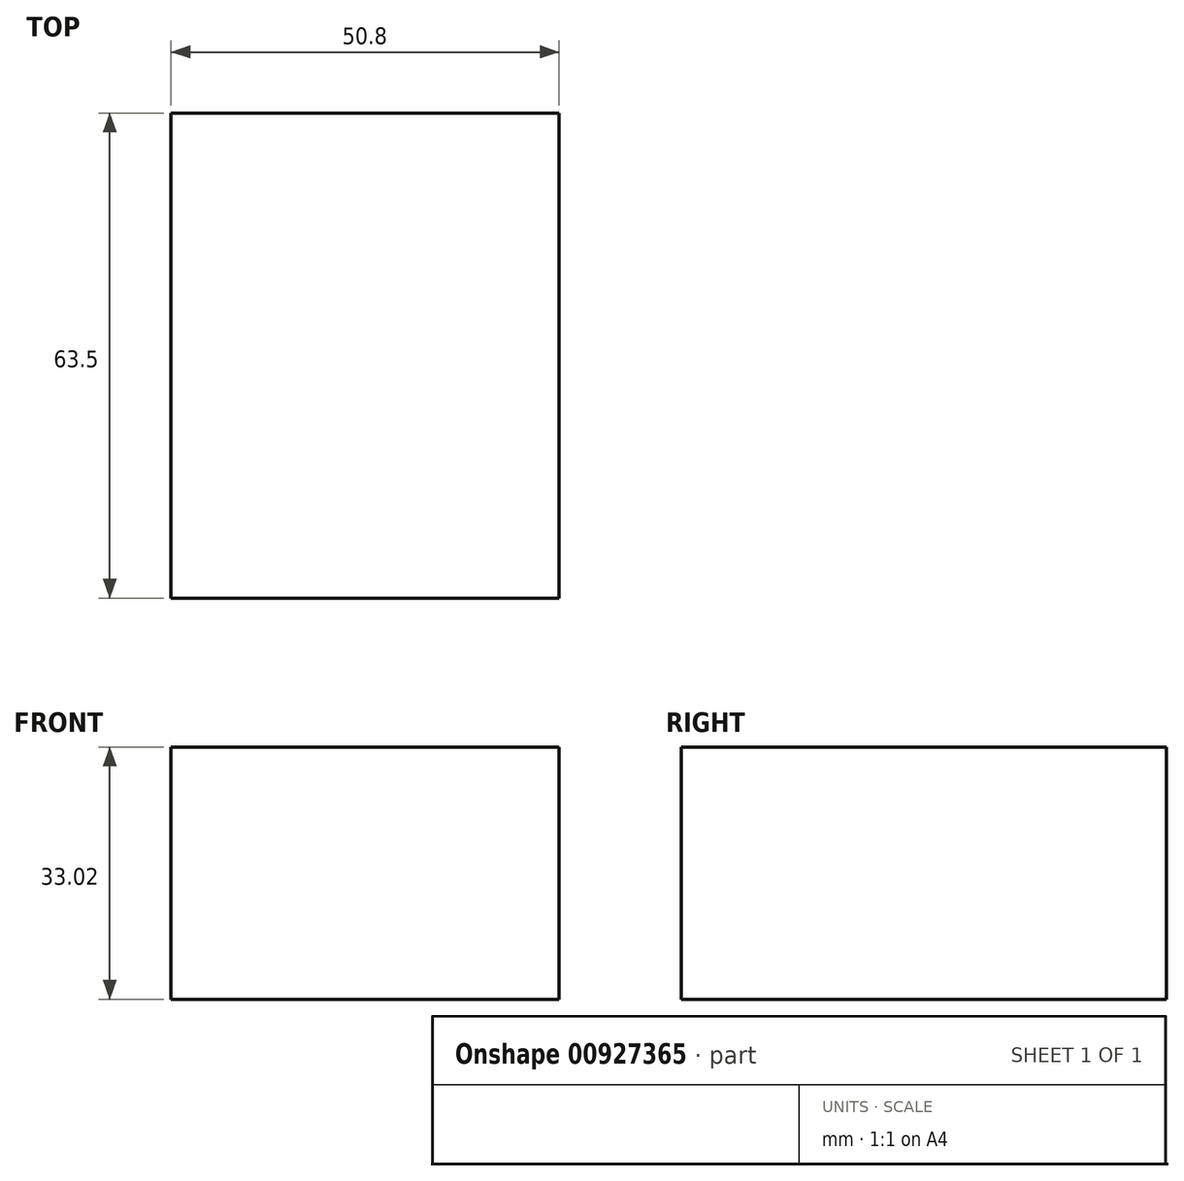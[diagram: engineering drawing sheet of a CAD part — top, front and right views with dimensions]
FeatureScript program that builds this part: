
annotation { "Feature Type Name" : "Feature", "Feature Type Description" : "" }
export const myFeature = defineFeature(function(context is Context, id is Id, definition is map)
    precondition{}
    {
        {
            var Q0;
            Q0=qCreatedBy(makeId("Top.planeOp"),FACE);
            var sketch = newSketch(context, id + "F0", { "sketchPlane" : qUnion([Q0])});
            skLineSegment(sketch, "E0.bottom", {"start": v(5.77, 0) * mm, "end": v(56.57, 0) * mm});
            skLineSegment(sketch, "E0.top", {"start": v(5.77, 63.5) * mm, "end": v(56.57, 63.5) * mm});
            skLineSegment(sketch, "E0.left", {"start": v(5.77, 0) * mm, "end": v(5.77, 63.5) * mm});
            skLineSegment(sketch, "E0.right", {"start": v(56.57, 0) * mm, "end": v(56.57, 63.5) * mm});
            skSolve(sketch);
        }
        {
            var Q0;
            Q0 = qSketchRegion(id + "F0", true);
            extrude(context, id + "F1", {"entities" : qUnion([Q0]), "depth" : 7.62 * mm, "offsetDistance" : 25.4 * mm});
        }
        {
            var Q0;
            Q0=makeQuery(id+"F1.opExtrude","CAP_FACE",FACE,{"disambiguationData":[OSD([sQuery(id+"F0.wireOp",EDGE,"E0.bottom"),sQuery(id+"F0.wireOp",EDGE,"E0.top"),sQuery(id+"F0.wireOp",EDGE,"E0.left"),sQuery(id+"F0.wireOp",EDGE,"E0.right")])],"isStart":false});
            var sketch = newSketch(context, id + "F2", { "sketchPlane" : qUnion([Q0])});
            skSolve(sketch);
        }
        {
            var Q0;
            Q0=makeQuery(id+"F2.imprint","IMPRINT",FACE,{"disambiguationData":[TD([[makeQuery(id+"F2.imprint","IMPRINT",EDGE,{"derivedFrom":makeQuery(id+"F1.opExtrude","CAP_EDGE",EDGE,{"disambiguationData":[OSD([sQuery(id+"F0.wireOp",EDGE,"E0.bottom")])],"isStart":false})}),1.0]])]});
            var sketch = newSketch(context, id + "F3", { "sketchPlane" : qUnion([Q0])});
            skText(sketch, "E1", { "text": "A", "fontName": "OpenSans-Italic.ttf"});
            skText(sketch, "E2", { "text": "M", "fontName": "OpenSans-Regular.ttf"});
            skText(sketch, "E3", { "text": "P", "fontName": "OpenSans-Regular.ttf"});
            const initialGuessF3  = {"E1": [0.01656, 0.0039, 1, 0, 0.01285], "E2": [0.0278, 0.00447, 1, 0, 0.01227], "E3": [0.04263, 0.00447, 1, 0, 0.01227]};
            skSetInitialGuess(sketch, initialGuessF3);
            skSolve(sketch);
        }
        {
            var Q0;
            Q0=makeQuery(id+"F2.imprint","IMPRINT",FACE,{"disambiguationData":[TD([[makeQuery(id+"F2.imprint","IMPRINT",EDGE,{"derivedFrom":makeQuery(id+"F1.opExtrude","CAP_EDGE",EDGE,{"disambiguationData":[OSD([sQuery(id+"F0.wireOp",EDGE,"E0.bottom")])],"isStart":false})}),1.0]])]});
            var Q1;
            Q1 = qSketchRegion(id + "F3", true);
            var Q2;
            Q2=makeQuery(id+"F3.imprint","IMPRINT",FACE,{"disambiguationData":[TD([[makeQuery(id+"F3.imprint","IMPRINT",EDGE,{"derivedFrom":sQuery(id+"F3.wireOp",EDGE,"E1.sketch_text.stroke-0")}),-1.0]])]});
            var Q3;
            Q3=makeQuery(id+"F3.imprint","IMPRINT",FACE,{"disambiguationData":[TD([[makeQuery(id+"F3.imprint","IMPRINT",EDGE,{"derivedFrom":sQuery(id+"F3.wireOp",EDGE,"E1.sketch_text.stroke-8")}),1.0]])]});
            var Q4;
            Q4=makeQuery(id+"F3.imprint","IMPRINT",FACE,{"disambiguationData":[TD([[makeQuery(id+"F3.imprint","IMPRINT",EDGE,{"derivedFrom":sQuery(id+"F3.wireOp",EDGE,"E1.sketch_text.stroke-0")}),1.0]])]});
            var Q5;
            Q5=makeQuery(id+"F1.opExtrude","CAP_FACE",FACE,{"disambiguationData":[OSD([sQuery(id+"F0.wireOp",EDGE,"E0.bottom"),sQuery(id+"F0.wireOp",EDGE,"E0.top"),sQuery(id+"F0.wireOp",EDGE,"E0.left"),sQuery(id+"F0.wireOp",EDGE,"E0.right")])],"isStart":false});
            var Q6;
            Q6=makeQuery(id+"F1.opExtrude","CAP_FACE",FACE,{"disambiguationData":[OSD([sQuery(id+"F0.wireOp",EDGE,"E0.bottom"),sQuery(id+"F0.wireOp",EDGE,"E0.top"),sQuery(id+"F0.wireOp",EDGE,"E0.left"),sQuery(id+"F0.wireOp",EDGE,"E0.right")])],"isStart":true});
            extrude(context, id + "F4", {"entities" : qUnion([Q0, Q1, Q2, Q3, Q4, Q5, Q6]), "operationType" : NewBodyOperationType.ADD, "oppositeDirection" : true, "depth" : 25.4 * mm, "offsetDistance" : 25.4 * mm});
        }
    });
